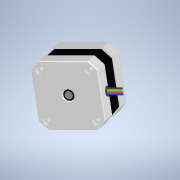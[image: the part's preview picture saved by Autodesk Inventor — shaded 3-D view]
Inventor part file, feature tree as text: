
AUTODESK INVENTOR PART (.ipt)
format: ipt  version: 2022 (Build 260153000, 153)  size: 910,848 bytes
history: native  units: mm
features: extrude x12, sketch x5, hole x4, fillet x4, plane x2, chamfer x1, pattern_linear x1, projected_geometry x1
ambient origin geometry x8: Origin, YZ Plane, XZ Plane, XY Plane, X Axis, Y Axis, Z Axis, Center Point
bodies: Solid1 (feature_tree)
feature tree (30):
  sketch  "Sketch1"  dims[d0=7.0mm d1=22.0mm]
  extrude  "Extrusion2"  Depth=22.0mm
  extrude  "Extrusion3"  Depth=5.0mm
  plane  "Work Plane2"
  extrude  "Extrusion7"  Depth=3.0mm
  extrude  "Extrusion8"  Depth=3.0mm
  chamfer  "Chamfer1"  Distance=42.0mm
  pattern_linear  "Rectangular Pattern2"  Spacing1=42.0mm  [1 undecoded]
  hole  "Hole1"  [1 undecoded]
  hole  "Hole2"  [1 undecoded]
  hole  "Hole3"  [1 undecoded]
  hole  "Hole4"  [1 undecoded]
  extrude  "Extrusion9"  Depth=2.0mm
  fillet  "Fillet1"  Radius=2.0mm
  fillet  "Fillet2"  Radius=48.0mm
  fillet  "Fillet3"  [1 undecoded]
  sketch  "Sketch6"  dims[d10=3.0mm d11=3.0mm]
  extrude  "Extrusion10"  Depth=2.0mm TaperAngle=0.0deg
  fillet  "Fillet4"  Radius=1.0mm
  extrude  "Extrusion11"  Depth=1.0mm
  extrude  "Extrusion12"  Depth=0.5mm
  extrude  "Extrusion13"  Depth=0.5mm
  extrude  "Extrusion14"  Depth=0.5mm
  extrude  "Extrusion15"  Depth=0.5mm
  plane  "Work Plane3"
  extrude  "Extrusion16"  Depth=0.5mm
  sketch  "Sketch4"  dims[d4=5.0mm d5=31.0mm]
  projected_geometry  "Projected Loop2"
  sketch  "Sketch5"  dims[d6=31.0mm d9=3.0mm]
  sketch  "Sketch11"  dims[d12=3.0mm d39=42.0mm d40=42.0mm d41=135.0deg d42=51.618795mm d43=51.618795mm d44=25.809398mm d45=25.809398mm d48=2.0mm d49=0.0mm d50=48.0mm d51=0.0mm d60=-10.0mm d126=28.0mm d127=0.0mm d128=1.0mm d129=1.0mm d130=1.0mm d131=1.0mm d132=0.5mm d134=0.5mm d135=0.5mm d136=0.5mm d137=0.5mm d138=1.0mm d139=1.0mm d140=0.5mm d141=0.0mm d145=0.125mm d146=2.0mm d147=45.0deg d148=560.0mm d150=0.5mm d151=10.0mm d152=10.0mm d153=6.0mm d154=6.0mm d155=4.0mm d156=2.0mm d157=90.0deg d158=3.0mm d159=0.0mm d160=10.0mm d161=10.0mm d162=6.0mm d163=6.0mm d164=4.0mm d165=2.0mm d166=90.0deg d167=3.0mm d168=0.0mm d169=10.0mm d170=10.0mm d171=6.0mm d172=6.0mm d173=4.0mm d174=2.0mm d175=90.0deg d176=3.0mm d177=0.0mm d178=10.0mm d179=10.0mm d180=6.0mm d181=6.0mm d182=4.0mm d183=2.0mm d184=90.0deg d185=3.0mm d186=0.0mm d189=47.0mm d190=0.0mm d191=1.0mm d192=1.0mm d196=0.5mm d197=1.2mm d198=40.0mm d200=1.2mm d201=10.0mm d203=10.0mm d205=2.5mm d206=2.5mm d207=1.0mm d208=0.0mm d209=0.3mm d210=10.0mm d211=0.0mm d212=10.0mm d213=0.0mm d214=10.0mm d215=0.0mm d216=10.0mm d217=0.0mm d218=0.2mm d219=5.0mm d220=0.0mm d221=0.0mm d225=-24.0mm d226=80.0mm d227=80.0mm d228=27.956465mm d229=27.979816mm d230=2.0mm d231=0.0mm d232=50.0mm d233=0.0mm]
note: 6 required parameter values undecoded (feature->parameter linkage not recoverable at this tier; creation-order binding heuristic only, values carry confidence <= 0.55)
